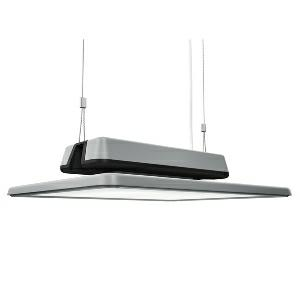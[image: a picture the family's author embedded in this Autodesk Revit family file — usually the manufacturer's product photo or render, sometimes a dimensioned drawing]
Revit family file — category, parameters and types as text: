
# Revit family: acaneo_-_hial_14000_850_n_dali_00737107_4336
name_source: partatom
category: Lighting Fixtures
units: mm (PartAtom-declared; Revit-internal decimal feet)

## family parameters
Cut with Voids When Loaded = No
Host = Face
Light Source = No
Part Type = Normal
Room Calculation Point = No
Round Connector Dimension = Use Diameter
Shared = No

## types (1)
- ACANEO - HIAL 14000/850/N/DALI (1 x LED, 15000 lm, 5000K)
    Apparent Load = 90 VA
    Approval mark = CE
    CIE Flux Codes = 84 97 100 100 100
    Color Rendering = 80-89
    Color Temperature = 5000K
    Control Gear = Electronic ballast
    Default Elevation = 1800 mm
    Description = HIAL 14000/850/N/DALI|High bay luminaire|light source: LED|work equipment: Adjustable electronic ballast, digital DALI|connected load: 220-240 V, 50/60 Hz|Power consumption: approx. 90 W|power factor: approx. 0,987|luminous flux: 15000 lm|luminous efficacy: 166 lm/W|colour temperature: Cold white, ca. 5000 K|color rendering index (CRI): >= 80|chromaticity tolerance:  3 SDCM|System of protection: IP 65|class of protection: I|technology: Continuously dimmable|luminaire body|material: Aluminium|surface: Powder coatet|colour: White aluminium|lamp cover: Acrylic (PMMA), Clear|weight (net): approx. 8.2 kg|mains lead: Built-in plug RST 20i5 Einbau|Fastening: Available separately|Accessory: Junction box (RST 20i5)|minimum ambient temperature: -30 ░C|maximum ambient temperature: 70 ░C|glare control: Optics|unified glare rating(4H 8H): <=  19|
    Frequency = 50 Hz, 60 Hz
    Height = 125 mm
    Lamp = 1 x LED
    Lamp Light Flux = 15000 lm
    Lamp count = 1
    Length = 480 mm
    Luminous efficacy = 167 lm/W
    Manufacturer = Waldmann
    ModVariant = No
    Model = 00737107
    Mounting Place = Ceiling
    Mounting Type = Pendant
    Number of Poles = 1
    OnlyDefault = Yes
    Power Factor = 1
    Product Name = ACANEO - HIAL 14000/850/N/DALI
    Product group = High bay luminaire (industry)
    ProductGroupID = 901
    Protection Class = Protection class I
    Protection Degree = IP 65
    RLX_Detail_Level = 1
    RLX_Emergency_Light_Flux = 0 lm
    RLX_Emergency_Type = 0
    RLX_Emergency_Type_DB = No
    RlxData = <blob elided: 30333 chars, md5=f68609e5>
    Socket = socket
    Standby Power = 0 W
    System Light Flux = 15000 lm
    System Power = 90 W
    Type Comments = Product without accessories
    Type Image = acaneo-hial.jpg
    URL = http://relux.com
    VarID = ---
    Voltage = 230 V
    Voltage Range = 110-120 V, 220-240 V
    Weight = 0.00 kg
    Width = 405 mm

## geometry (parser evidence)
native form markers: Blend x4, Sweep x10
no freeform markers — native parametric forms only
